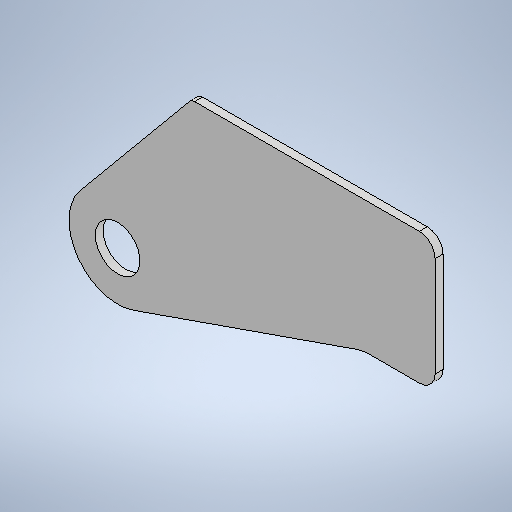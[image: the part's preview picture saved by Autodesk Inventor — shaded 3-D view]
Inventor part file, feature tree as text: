
AUTODESK INVENTOR PART (.ipt)
format: ipt  version: 2025 (Build 290162010, 162A)  size: 290,304 bytes
history: native  units: mm
features: other x2, sheet_metal_op x1, chamfer x1, sketch x1
ambient origin geometry x8: Origin, YZ Plane, XZ Plane, XY Plane, X Axis, Y Axis, Z Axis, Center Point
bodies: Solid1 (feature_tree)
feature tree (5):
  sheet_metal_op  "Face1"
  chamfer  "Corner Round3"
  sketch  "Sketch1"  dims[d2=80.0mm d3=40.0mm d6=3.0mm d29=5.0mm d30=17.0mm d31=10.0mm d32=40.0mm d34=5.0mm d35=15.0mm d36=25.0mm d37=6.0mm d38=5.0mm d41=66.357903mm]
  other  "Plate1"
  other  "Definition1"
